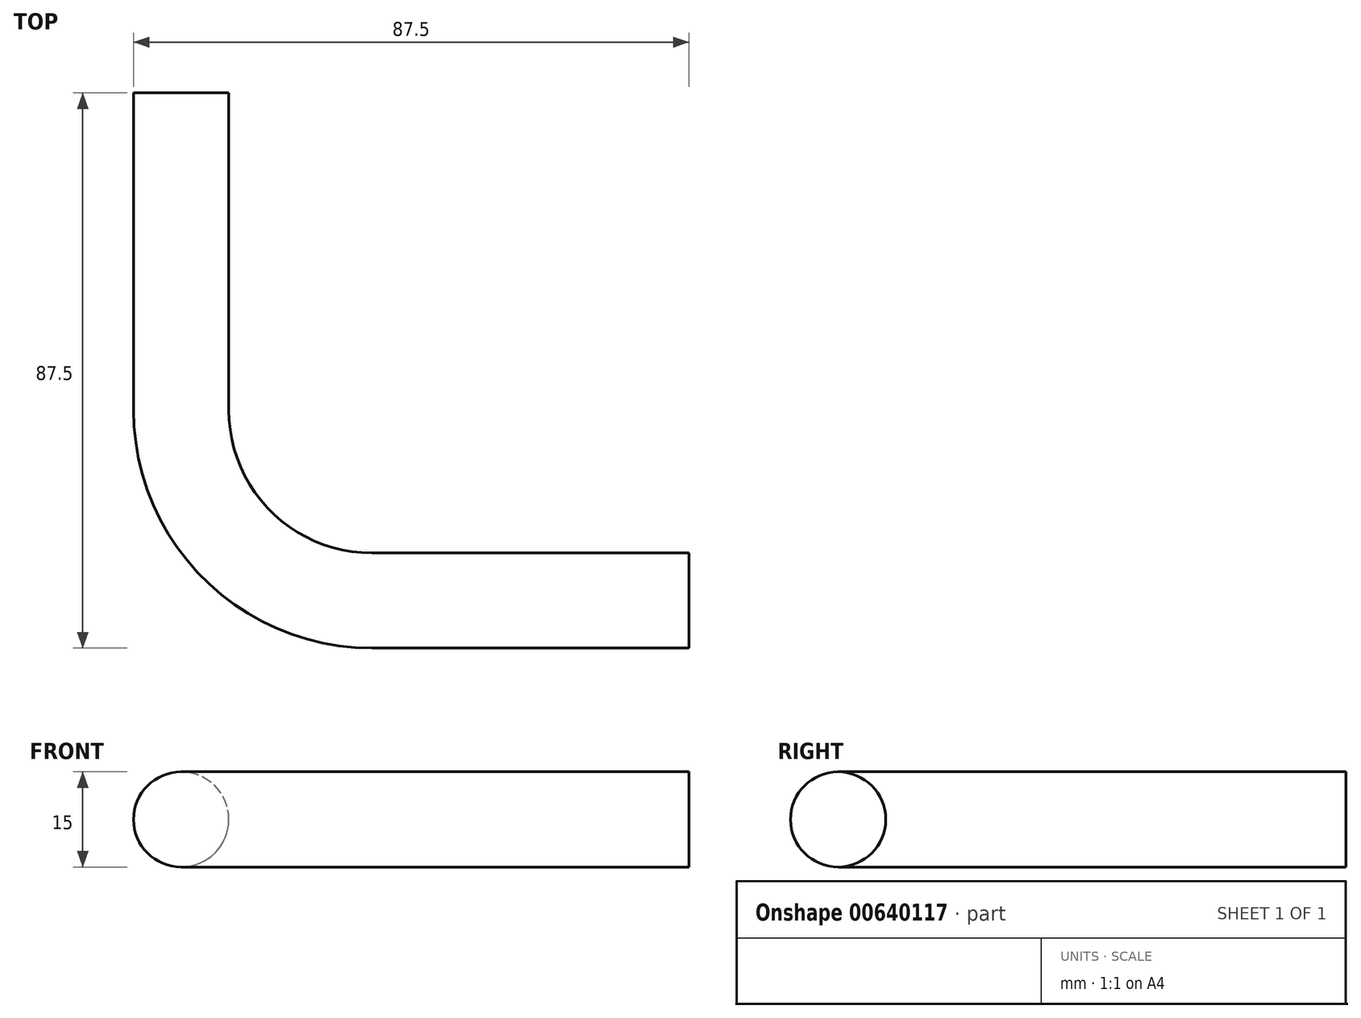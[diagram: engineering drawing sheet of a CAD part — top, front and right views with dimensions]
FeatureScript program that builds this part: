
annotation { "Feature Type Name" : "Feature", "Feature Type Description" : "" }
export const myFeature = defineFeature(function(context is Context, id is Id, definition is map)
    precondition{}
    {
        {
            var Q0;
            Q0=qCreatedBy(makeId("Top.planeOp"),FACE);
            var sketch = newSketch(context, id + "F0", { "sketchPlane" : qUnion([Q0])});
            skLineSegment(sketch, "E0", {"start": v(0, 0) * mm, "end": v(0, -50) * mm});
            skLineSegment(sketch, "E1", {"start": v(30, -80) * mm, "end": v(80, -80) * mm});
            skPoint(sketch, "E2.visualSharp", {"position": v(0, -80) * mm});
            skArc(sketch, "E2.filletArc", {"start": v(0, -50) * mm, "mid": v(8.79, -71.21) * mm, "end": v(30, -80) * mm});
            skSolve(sketch);
        }
        {
            var Q0;
            Q0=qCreatedBy(makeId("Front.planeOp"),FACE);
            var sketch = newSketch(context, id + "F1", { "sketchPlane" : qUnion([Q0])});
            skCircle(sketch, "E3", {"center": v(0, 0) * mm, "radius": 7.5 * mm});
            skSolve(sketch);
        }
        {
            var Q0;
            Q0=makeQuery(id+"F1.imprint","IMPRINT",FACE,{"disambiguationData":[TD([[makeQuery(id+"F1.imprint","IMPRINT",EDGE,{"derivedFrom":sQuery(id+"F1.wireOp",EDGE,"E3")}),1.0]])]});
            var Q1;
            Q1 = qConstructionFilter(qBodyType(qCreatedBy(id + "F0" ,EDGE), BodyType.WIRE), ConstructionObject.NO);
            sweep(context, id + "F2", {"profiles" : qUnion([Q0]), "path" : qUnion([Q1])});
        }
    });
